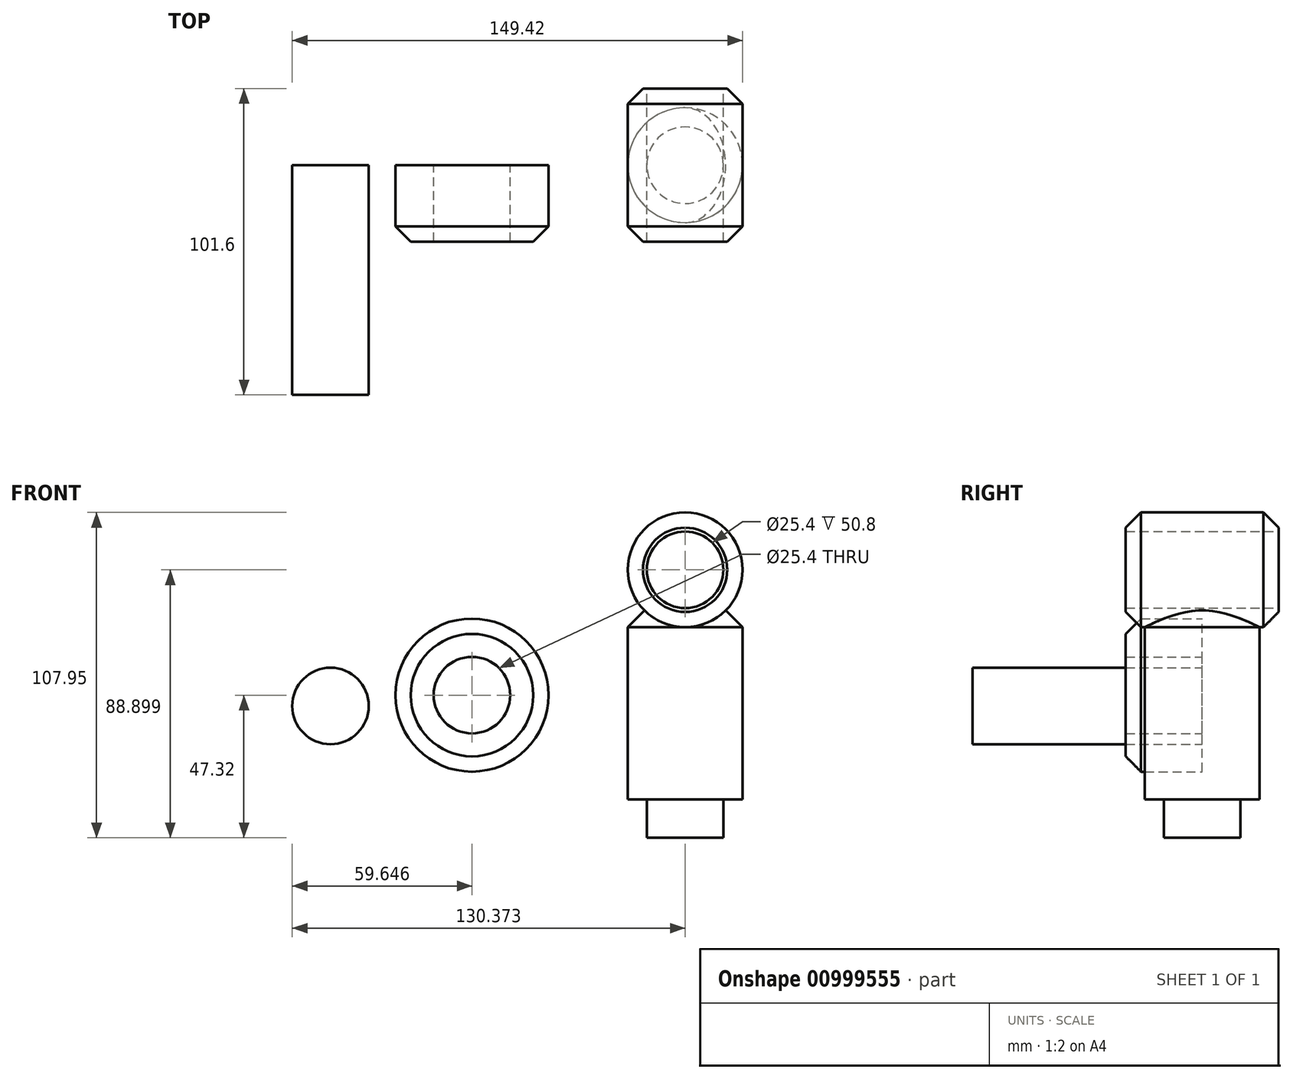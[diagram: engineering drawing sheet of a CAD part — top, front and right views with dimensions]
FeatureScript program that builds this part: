
annotation { "Feature Type Name" : "Feature", "Feature Type Description" : "" }
export const myFeature = defineFeature(function(context is Context, id is Id, definition is map)
    precondition{}
    {
        {
            var Q0;
            Q0=qCreatedBy(makeId("Front.planeOp"),FACE);
            var sketch = newSketch(context, id + "F0", { "sketchPlane" : qUnion([Q0])});
            skCircle(sketch, "E0", {"center": v(-25.17, 3.6) * mm, "radius": 12.7 * mm});
            skCircle(sketch, "E1", {"center": v(-25.17, 3.6) * mm, "radius": 25.4 * mm});
            skLineSegment(sketch, "E2", {"start": v(45.55, 26.12) * mm, "end": v(45.55, -31.03) * mm});
            skLineSegment(sketch, "E3", {"start": v(45.55, -31.03) * mm, "end": v(45.55, -43.73) * mm});
            skLineSegment(sketch, "E4.bottom", {"start": v(45.55, -31.03) * mm, "end": v(58.25, -31.03) * mm});
            skLineSegment(sketch, "E4.top", {"start": v(45.55, -43.73) * mm, "end": v(58.25, -43.73) * mm});
            skLineSegment(sketch, "E4.right", {"start": v(58.25, -31.03) * mm, "end": v(58.25, -43.73) * mm});
            skLineSegment(sketch, "E5.top", {"start": v(45.55, -31.03) * mm, "end": v(64.6, -31.03) * mm});
            skLineSegment(sketch, "E5.right", {"start": v(64.6, 26.12) * mm, "end": v(64.6, -31.03) * mm});
            skArc(sketch, "E6", {"start": v(45.55, 26.12) * mm, "mid": v(64.6, 45.17) * mm, "end": v(45.55, 64.22) * mm});
            skArc(sketch, "E7", {"start": v(45.55, 32.47) * mm, "mid": v(58.25, 45.17) * mm, "end": v(45.55, 57.87) * mm});
            skLineSegment(sketch, "E8", {"start": v(59.02, 31.7) * mm, "end": v(64.6, 26.12) * mm});
            skLineSegment(sketch, "E9", {"start": v(59.02, 31.7) * mm, "end": v(45.55, 26.12) * mm});
            skLineSegment(sketch, "E10", {"start": v(45.55, 26.12) * mm, "end": v(45.55, 64.22) * mm});
            skSolve(sketch);
        }
        {
            var Q0;
            Q0=makeQuery(id+"F0.imprint","IMPRINT",FACE,{"disambiguationData":[TD([[makeQuery(id+"F0.imprint","IMPRINT",EDGE,{"derivedFrom":sQuery(id+"F0.wireOp",EDGE,"E0")}),-1.0]])]});
            extrude(context, id + "F1", {"entities" : qUnion([Q0]), "depth" : 25.4 * mm, "offsetDistance" : 25.4 * mm});
        }
        {
            var Q0;
            Q0=makeQuery(id+"F1.opExtrude","CAP_EDGE",EDGE,{"disambiguationData":[OSD([sQuery(id+"F0.wireOp",EDGE,"E1")])],"isStart":false});
            chamfer(context, id + "F2", {"entities" : qUnion([Q0]), "width" : 5.08 * mm, "tangentPropagation" : true});
        }
        {
            var Q0;
            {var subQ0=sQuery(id+"F0.wireOp",EDGE,"E9");Q0=makeQuery(id+"F0.imprint","IMPRINT",FACE,{"disambiguationData":[TD([[makeQuery(id+"F0.imprint","IMPRINT",EDGE,{"derivedFrom":subQ0}),1.0]])]});}
            var Q1;
            {var subQ1=sQuery(id+"F0.wireOp",EDGE,"E7");Q1=makeQuery(id+"F0.imprint","IMPRINT",FACE,{"disambiguationData":[TD([[makeQuery(id+"F0.imprint","IMPRINT",EDGE,{"derivedFrom":subQ1}),-1.0]])]});}
            extrude(context, id + "F3", {"entities" : qUnion([Q0, Q1]), "endBound" : BoundingType.SYMMETRIC, "depth" : 50.8 * mm, "offsetDistance" : 25.4 * mm});
        }
        {
            var Q0;
            Q0=makeQuery(id+"F3.opExtrude","SWEPT_BODY",BODY,{"disambiguationData":[OSD([sQuery(id+"F0.wireOp",EDGE,"E6"),sQuery(id+"F0.wireOp",EDGE,"E7"),sQuery(id+"F0.wireOp",EDGE,"E10")])]});
            var Q1;
            {var subQ0=sQuery(id+"F0.wireOp",EDGE,"E10");Q1=makeQuery(id+"F3.opExtrude","SWEPT_FACE",FACE,{"disambiguationData":[OSD([subQ0]),TDD([makeQuery(id+"F0.imprint","IMPRINT",EDGE,{"disambiguationData":[TD([[makeQuery(id+"F0.imprint","INTERSECT",VERTEX,{"disambiguationData":[OD(0.0)],"derivedFrom":[sQuery(id+"F0.wireOp",EDGE,"E7"),subQ0]}),1.0]])],"derivedFrom":subQ0})])]});}
            mirror(context, id + "F4", {"operationType" : NewBodyOperationType.ADD, "entities" : qUnion([Q0]), "mirrorPlane" : qUnion([Q1])});
        }
        {
            var Q0;
            {var subQ0=sQuery(id+"F0.wireOp",EDGE,"E2");Q0=makeQuery(id+"F0.imprint","IMPRINT",FACE,{"disambiguationData":[TD([[makeQuery(id+"F0.imprint","IMPRINT",EDGE,{"derivedFrom":subQ0}),1.0]])]});}
            var Q1;
            Q1=makeQuery(id+"F0.imprint","IMPRINT",FACE,{"disambiguationData":[TD([[makeQuery(id+"F0.imprint","IMPRINT",EDGE,{"derivedFrom":sQuery(id+"F0.wireOp",EDGE,"E3")}),1.0]])]});
            var Q2;
            Q2=sQuery(id+"F0.wireOp",EDGE,"E2");
            revolve(context, id + "F5", {"operationType" : NewBodyOperationType.ADD, "surfaceOperationType" : NewSurfaceOperationType.NEW, "entities" : qUnion([Q0, Q1]), "axis" : qUnion([Q2]), "revolveType" : RevolveType.FULL});
        }
        {
            var Q0;
            {var subQ0=makeQuery(id+"F3.opExtrude","CAP_EDGE",EDGE,{"disambiguationData":[OSD([sQuery(id+"F0.wireOp",EDGE,"E6")])],"isStart":false});Q0=makeQuery(id+"F4.boolean.opBoolean","MERGE",EDGE,{"derivedFrom":[subQ0,makeQuery(id+"F4.opPattern","COPY",EDGE,{"derivedFrom":subQ0,"instanceName":"1"})]});}
            var Q1;
            {var subQ0=makeQuery(id+"F3.opExtrude","CAP_EDGE",EDGE,{"disambiguationData":[OSD([sQuery(id+"F0.wireOp",EDGE,"E6")])],"isStart":true});Q1=makeQuery(id+"F4.boolean.opBoolean","MERGE",EDGE,{"derivedFrom":[subQ0,makeQuery(id+"F4.opPattern","COPY",EDGE,{"derivedFrom":subQ0,"instanceName":"1"})]});}
            chamfer(context, id + "F6", {"entities" : qUnion([Q0, Q1]), "width" : 5.08 * mm, "tangentPropagation" : true});
        }
        {
            var Q0;
            Q0=qCreatedBy(makeId("Front.planeOp"),FACE);
            var sketch = newSketch(context, id + "F7", { "sketchPlane" : qUnion([Q0])});
            skCircle(sketch, "E11", {"center": v(-72.12, 0) * mm, "radius": 12.7 * mm});
            skSolve(sketch);
        }
        {
            var Q0;
            Q0=makeQuery(id+"F7.imprint","IMPRINT",FACE,{"disambiguationData":[TD([[makeQuery(id+"F7.imprint","IMPRINT",EDGE,{"derivedFrom":sQuery(id+"F7.wireOp",EDGE,"E11")}),1.0]])]});
            extrude(context, id + "F8", {"entities" : qUnion([Q0]), "depth" : 76.2 * mm, "offsetDistance" : 25.4 * mm});
        }
    });
